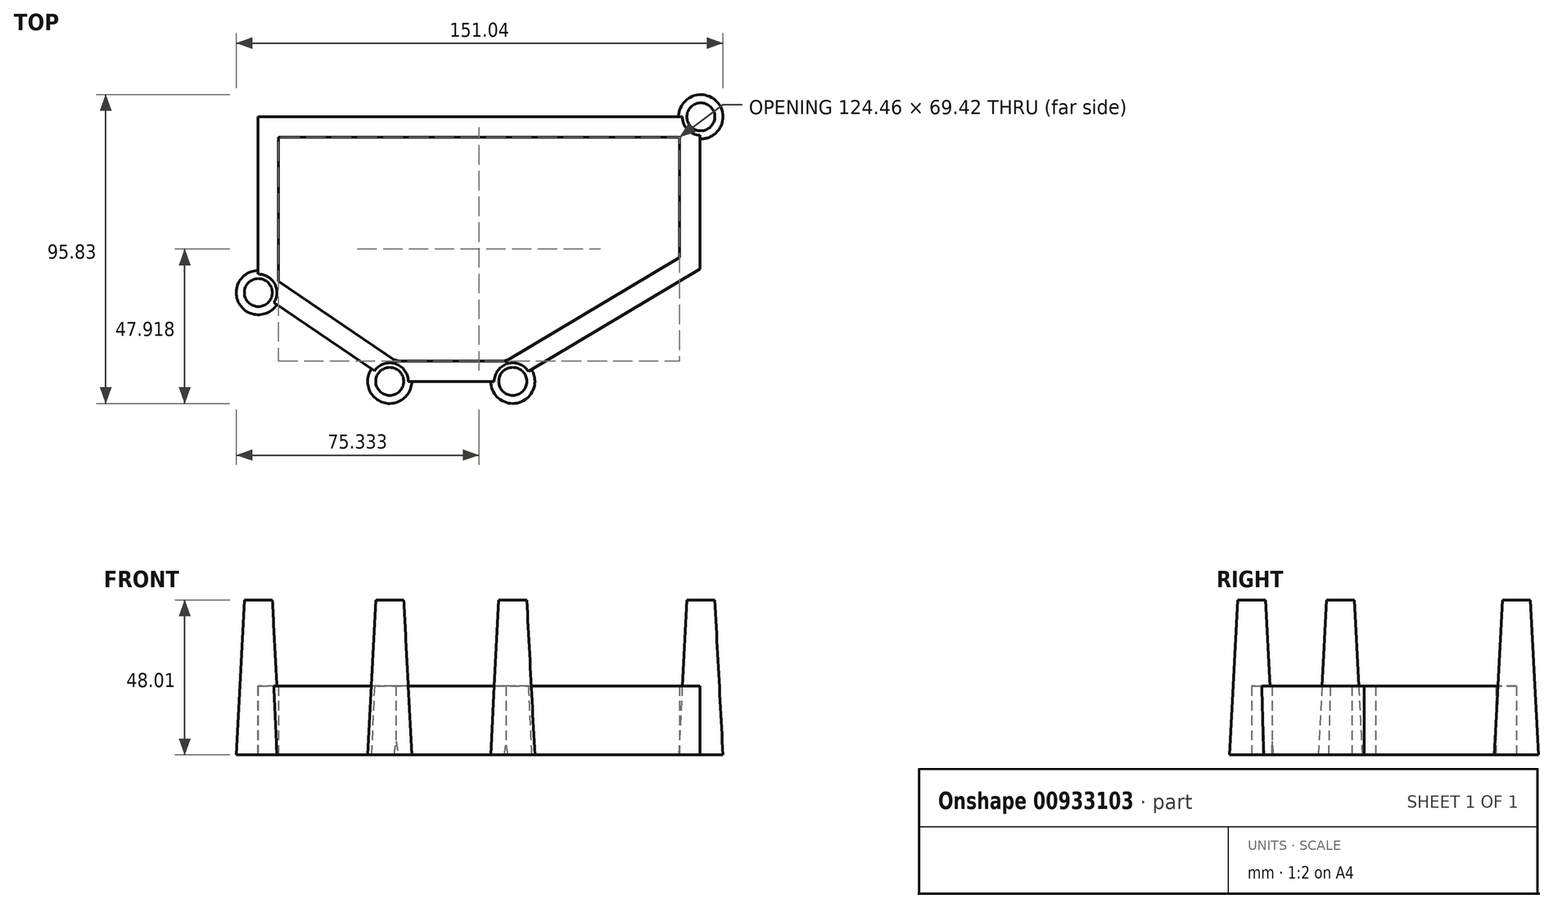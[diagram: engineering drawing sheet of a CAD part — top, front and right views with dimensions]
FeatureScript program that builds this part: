
annotation { "Feature Type Name" : "Feature", "Feature Type Description" : "" }
export const myFeature = defineFeature(function(context is Context, id is Id, definition is map)
    precondition{}
    {
        {
            var Q0;
            Q0=qCreatedBy(makeId("Top.planeOp"),FACE);
            var sketch = newSketch(context, id + "F0", { "sketchPlane" : qUnion([Q0])});
            skLineSegment(sketch, "E0", {"start": v(-40.89, 82.12) * mm, "end": v(96.27, 82.12) * mm});
            skLineSegment(sketch, "E1", {"start": v(96.27, 82.12) * mm, "end": v(96.27, 34.85) * mm});
            skLineSegment(sketch, "E2", {"start": v(96.27, 34.85) * mm, "end": v(37.78, 0) * mm});
            skLineSegment(sketch, "E3", {"start": v(37.78, 0) * mm, "end": v(0, 0) * mm});
            skLineSegment(sketch, "E4", {"start": v(0, 0) * mm, "end": v(-40.89, 27.76) * mm});
            skLineSegment(sketch, "E5", {"start": v(-40.89, 27.76) * mm, "end": v(-40.89, 82.12) * mm});
            skLineSegment(sketch, "E6.0", {"start": v(89.92, 38.45) * mm, "end": v(36.03, 6.35) * mm});
            skLineSegment(sketch, "E6.1", {"start": v(1.95, 6.35) * mm, "end": v(-34.54, 31.12) * mm});
            skLineSegment(sketch, "E6.2", {"start": v(-34.54, 31.12) * mm, "end": v(-34.54, 75.77) * mm});
            skLineSegment(sketch, "E6.3", {"start": v(36.03, 6.35) * mm, "end": v(1.95, 6.35) * mm});
            skLineSegment(sketch, "E6.4", {"start": v(-34.54, 75.77) * mm, "end": v(89.92, 75.77) * mm});
            skLineSegment(sketch, "E6.5", {"start": v(89.92, 75.77) * mm, "end": v(89.92, 38.45) * mm});
            skSolve(sketch);
        }
        {
            var Q0;
            Q0 = qSketchRegion(id + "F0", true);
            extrude(context, id + "F1", {"entities" : qUnion([Q0]), "depth" : 21.34 * mm, "offsetDistance" : 25.4 * mm});
        }
        {
            var Q0;
            Q0=qCreatedBy(makeId("Top.planeOp"),FACE);
            var sketch = newSketch(context, id + "F2", { "sketchPlane" : qUnion([Q0])});
            skCircle(sketch, "E7", {"center": v(0, 0) * mm, "radius": 6.86 * mm});
            skCircle(sketch, "E8", {"center": v(38.18, 0) * mm, "radius": 6.86 * mm});
            skCircle(sketch, "E9", {"center": v(96.53, 82.1) * mm, "radius": 6.86 * mm});
            skCircle(sketch, "E10", {"center": v(-40.78, 27.55) * mm, "radius": 6.86 * mm});
            skSolve(sketch);
        }
        {
            var Q0;
            Q0 = qSketchRegion(id + "F2", true);
            extrude(context, id + "F3", {"entities" : qUnion([Q0]), "operationType" : NewBodyOperationType.ADD, "depth" : 48 * mm, "offsetDistance" : 25.4 * mm, "hasDraft" : true, "draftAngle" : 3 * degree, "draftPullDirection" : true});
        }
    });
